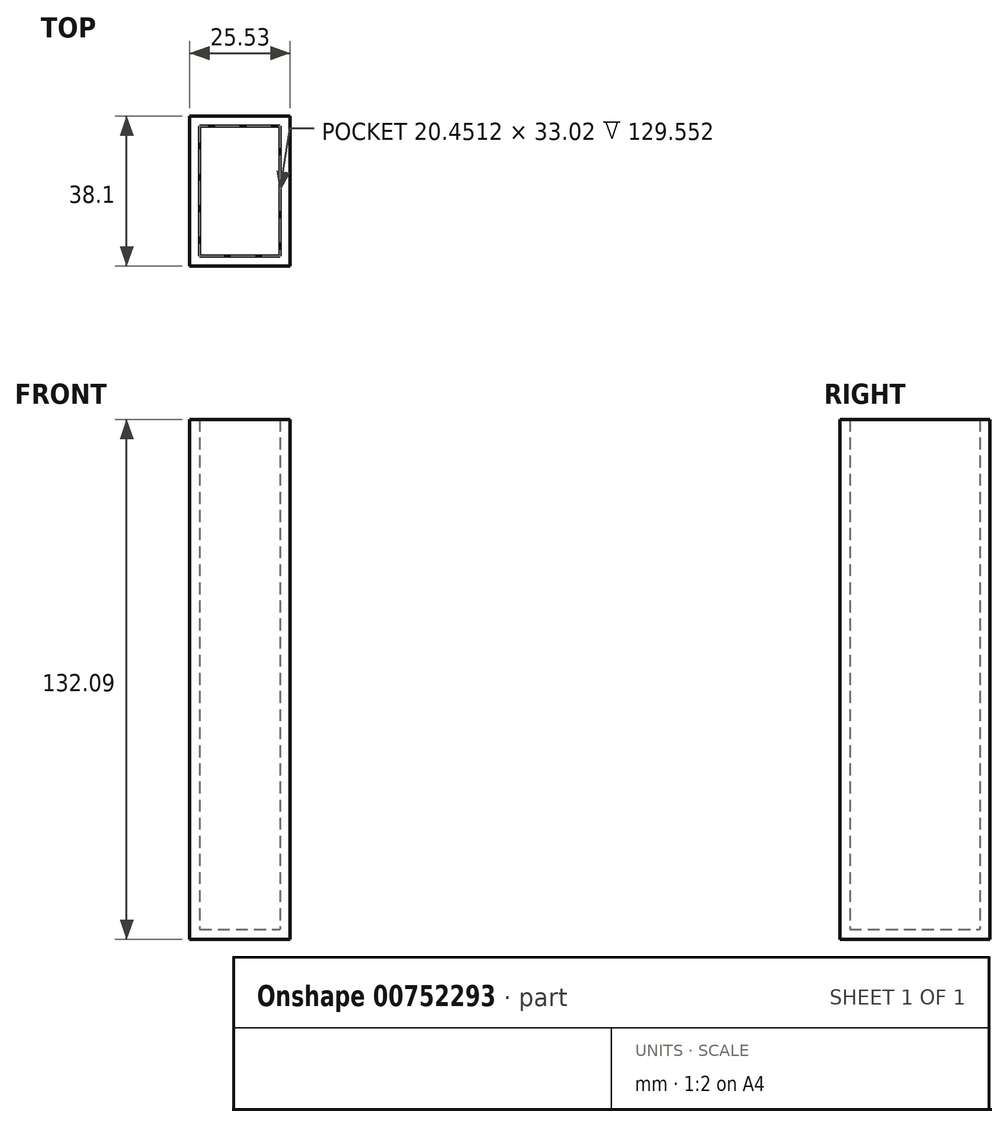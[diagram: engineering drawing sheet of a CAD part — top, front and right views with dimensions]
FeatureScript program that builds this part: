
annotation { "Feature Type Name" : "Feature", "Feature Type Description" : "" }
export const myFeature = defineFeature(function(context is Context, id is Id, definition is map)
    precondition{}
    {
        {
            var Q0;
            Q0=qCreatedBy(makeId("Front.planeOp"),FACE);
            var sketch = newSketch(context, id + "F0", { "sketchPlane" : qUnion([Q0])});
            skLineSegment(sketch, "E0.bottom", {"start": v(0, 0) * mm, "end": v(25.53, 0) * mm});
            skLineSegment(sketch, "E0.top", {"start": v(0, -132.1) * mm, "end": v(25.53, -132.1) * mm});
            skLineSegment(sketch, "E0.left", {"start": v(0, 0) * mm, "end": v(0, -132.1) * mm});
            skLineSegment(sketch, "E0.right", {"start": v(25.53, 0) * mm, "end": v(25.53, -132.1) * mm});
            skSolve(sketch);
        }
        {
            var Q0;
            Q0=makeQuery(id+"F0.imprint","IMPRINT",FACE,{"disambiguationData":[TD([[makeQuery(id+"F0.imprint","IMPRINT",EDGE,{"derivedFrom":sQuery(id+"F0.wireOp",EDGE,"E0.bottom")}),-1.0]])]});
            extrude(context, id + "F1", {"entities" : qUnion([Q0]), "endBound" : BoundingType.SYMMETRIC, "depth" : 38.1 * mm, "offsetDistance" : 25.4 * mm});
        }
        {
            var Q0;
            Q0=makeQuery(id+"F1.opExtrude","SWEPT_FACE",FACE,{"disambiguationData":[OSD([sQuery(id+"F0.wireOp",EDGE,"E0.bottom")])]});
            shell(context, id + "F2", {"entities" : qUnion([Q0]), "thickness" : 2.54 * mm});
        }
    });
